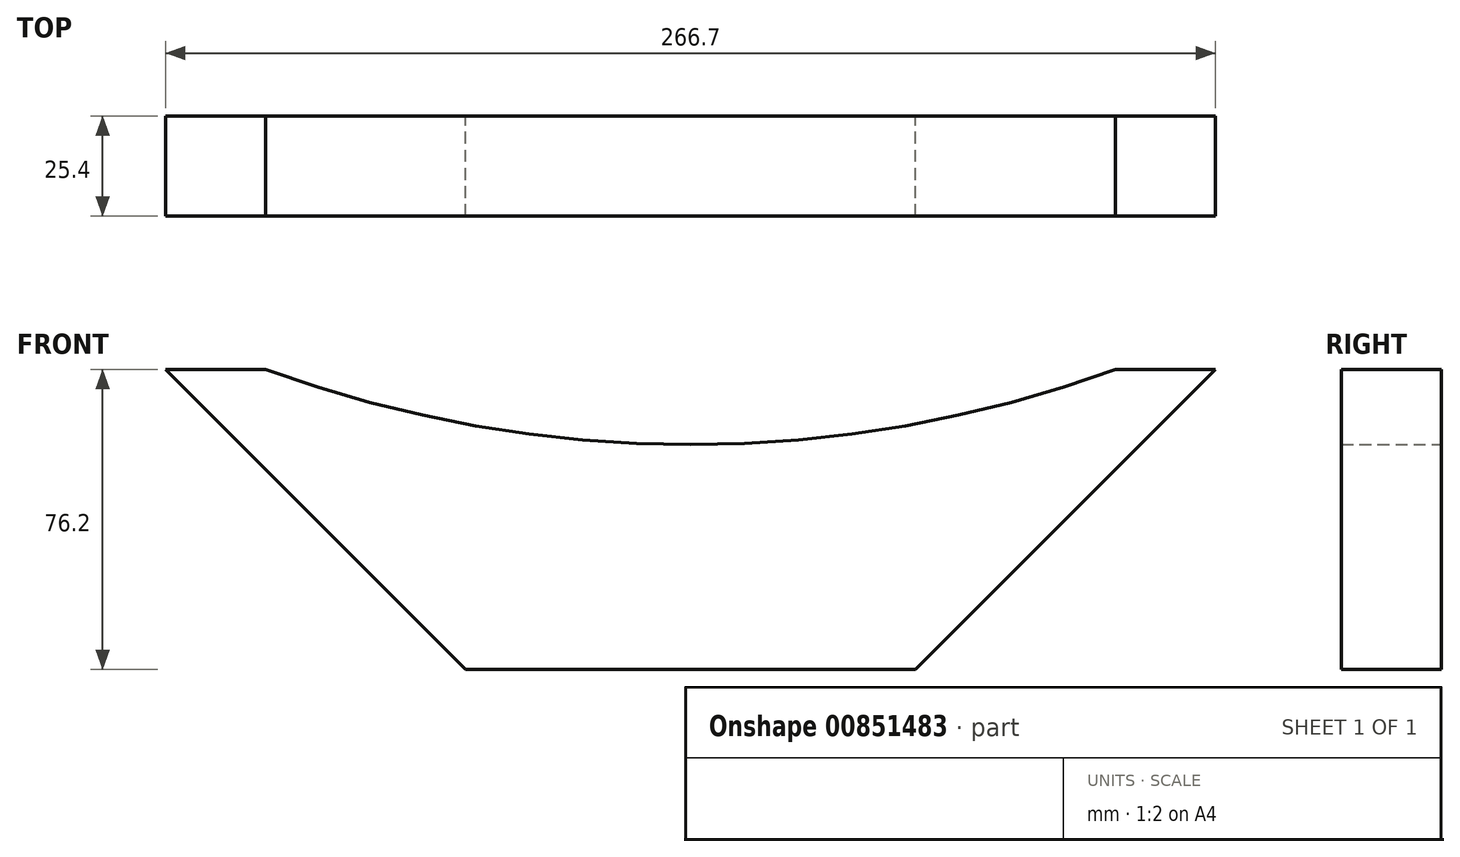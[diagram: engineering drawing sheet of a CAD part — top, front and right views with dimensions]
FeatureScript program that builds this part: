
annotation { "Feature Type Name" : "Feature", "Feature Type Description" : "" }
export const myFeature = defineFeature(function(context is Context, id is Id, definition is map)
    precondition{}
    {
        {
            var Q0;
            Q0=qCreatedBy(makeId("Front.planeOp"),FACE);
            var sketch = newSketch(context, id + "F0", { "sketchPlane" : qUnion([Q0])});
            skLineSegment(sketch, "E0.bottom", {"start": v(-153.02, 81.5) * mm, "end": v(-127.62, 81.5) * mm});
            skLineSegment(sketch, "E0.top", {"start": v(-76.82, 5.3) * mm, "end": v(37.48, 5.3) * mm});
            skArc(sketch, "E1", {"start": v(-127.62, 81.5) * mm, "mid": v(-19.67, 62.45) * mm, "end": v(88.28, 81.5) * mm});
            skPoint(sketch, "E2", {"position": v(-127.62, 81.5) * mm});
            skPoint(sketch, "E3", {"position": v(88.28, 81.5) * mm});
            skLineSegment(sketch, "E4.trimOffspring", {"start": v(88.28, 81.5) * mm, "end": v(113.68, 81.5) * mm});
            skLineSegment(sketch, "E5", {"start": v(-153.02, 81.5) * mm, "end": v(-76.82, 5.3) * mm});
            skLineSegment(sketch, "E6", {"start": v(113.68, 81.5) * mm, "end": v(37.48, 5.3) * mm});
            skSolve(sketch);
        }
        {
            var Q0;
            Q0 = qSketchRegion(id + "F0", true);
            extrude(context, id + "F1", {"entities" : qUnion([Q0]), "depth" : 25.4 * mm, "offsetDistance" : 25.4 * mm});
        }
    });
